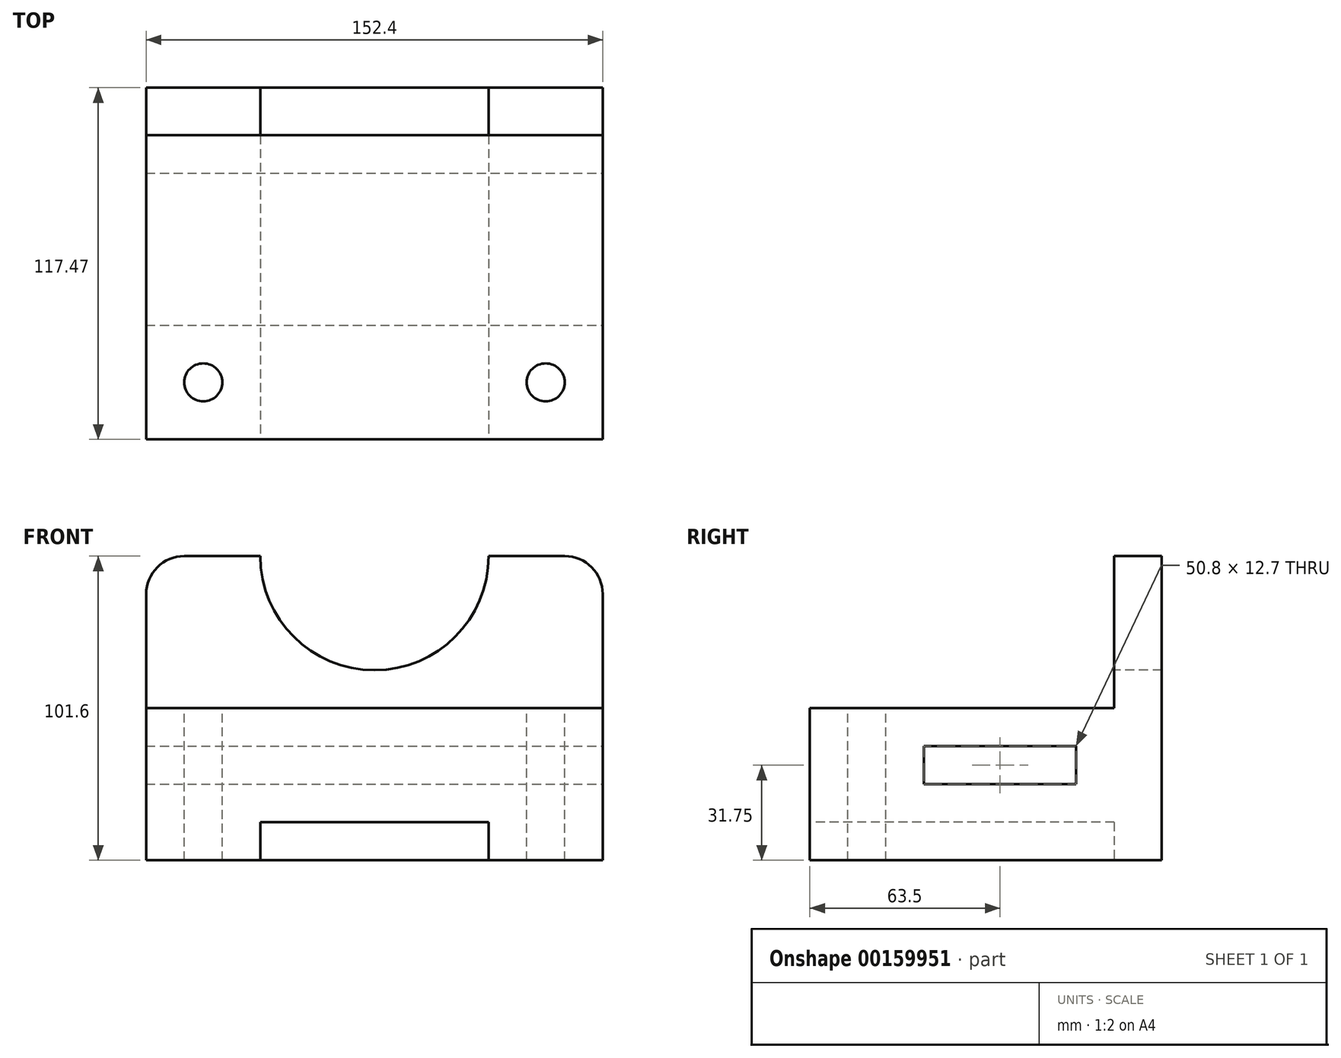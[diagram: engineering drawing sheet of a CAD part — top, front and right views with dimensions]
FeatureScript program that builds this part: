
annotation { "Feature Type Name" : "Feature", "Feature Type Description" : "" }
export const myFeature = defineFeature(function(context is Context, id is Id, definition is map)
    precondition{}
    {
        {
            var Q0;
            Q0=qCreatedBy(makeId("Front.planeOp"),FACE);
            var sketch = newSketch(context, id + "F0", { "sketchPlane" : qUnion([Q0])});
            skLineSegment(sketch, "E0.bottom", {"start": v(-76.2, 25.4) * mm, "end": v(76.2, 25.4) * mm});
            skLineSegment(sketch, "E0.top", {"start": v(-76.2, -25.4) * mm, "end": v(76.2, -25.4) * mm});
            skLineSegment(sketch, "E0.left", {"start": v(-76.2, 25.4) * mm, "end": v(-76.2, -25.4) * mm});
            skLineSegment(sketch, "E0.right", {"start": v(76.2, 25.4) * mm, "end": v(76.2, -25.4) * mm});
            skPoint(sketch, "E0.middle", {"position": v(0, 0) * mm});
            skLineSegment(sketch, "E1.bottom", {"start": v(-38.1, -12.7) * mm, "end": v(38.1, -12.7) * mm});
            skLineSegment(sketch, "E1.top", {"start": v(-38.1, -25.4) * mm, "end": v(38.1, -25.4) * mm});
            skLineSegment(sketch, "E1.left", {"start": v(-38.1, -12.7) * mm, "end": v(-38.1, -25.4) * mm});
            skLineSegment(sketch, "E1.right", {"start": v(38.1, -12.7) * mm, "end": v(38.1, -25.4) * mm});
            skSolve(sketch);
        }
        {
            var Q0;
            Q0=makeQuery(id+"F0.imprint","IMPRINT",FACE,{"disambiguationData":[TD([[makeQuery(id+"F0.imprint","IMPRINT",EDGE,{"derivedFrom":sQuery(id+"F0.wireOp",EDGE,"E0.bottom")}),-1.0]])]});
            extrude(context, id + "F1", {"entities" : qUnion([Q0]), "oppositeDirection" : true, "depth" : 101.6 * mm});
        }
        {
            var Q0;
            Q0=makeQuery(id+"F1.opExtrude","SWEPT_FACE",FACE,{"disambiguationData":[OSD([sQuery(id+"F0.wireOp",EDGE,"E0.right")])]});
            var sketch = newSketch(context, id + "F2", { "sketchPlane" : qUnion([Q0])});
            skLineSegment(sketch, "E2.bottom", {"start": v(38.1, 12.7) * mm, "end": v(88.9, 12.7) * mm});
            skLineSegment(sketch, "E2.top", {"start": v(38.1, 0) * mm, "end": v(88.9, 0) * mm});
            skLineSegment(sketch, "E2.left", {"start": v(38.1, 12.7) * mm, "end": v(38.1, 0) * mm});
            skLineSegment(sketch, "E2.right", {"start": v(88.9, 12.7) * mm, "end": v(88.9, 0) * mm});
            skLineSegment(sketch, "E3.bottom", {"start": v(53.98, 12.7) * mm, "end": v(73.03, 12.7) * mm});
            skLineSegment(sketch, "E3.top", {"start": v(53.98, 25.4) * mm, "end": v(73.03, 25.4) * mm});
            skLineSegment(sketch, "E3.left", {"start": v(53.98, 12.7) * mm, "end": v(53.98, 25.4) * mm});
            skLineSegment(sketch, "E3.right", {"start": v(73.03, 12.7) * mm, "end": v(73.03, 25.4) * mm});
            skSolve(sketch);
        }
        {
            var Q0;
            Q0=makeQuery(id+"F2.imprint","IMPRINT",FACE,{"disambiguationData":[TD([[makeQuery(id+"F2.imprint","IMPRINT",EDGE,{"derivedFrom":sQuery(id+"F2.wireOp",EDGE,"E2.bottom")}),-1.0]])]});
            var Q1;
            Q1=makeQuery(id+"F2.imprint","IMPRINT",FACE,{"disambiguationData":[TD([[makeQuery(id+"F2.imprint","IMPRINT",EDGE,{"derivedFrom":sQuery(id+"F2.wireOp",EDGE,"E3.bottom")}),1.0]])]});
            extrude(context, id + "F3", {"entities" : qUnion([Q0, Q1]), "operationType" : NewBodyOperationType.REMOVE, "oppositeDirection" : true, "depth" : 152.4 * mm});
        }
        {
            var Q0;
            {var subQ2=sQuery(id+"F0.wireOp",EDGE,"E0.bottom");Q0=makeQuery(id+"F3.boolean.opBoolean","SPLIT",FACE,{"disambiguationData":[TD([makeQuery(id+"F3.opExtrude","SWEPT_FACE",FACE,{"disambiguationData":[OSD([sQuery(id+"F2.wireOp",EDGE,"E3.left")])]})])],"derivedFrom":makeQuery(id+"F1.opExtrude","SWEPT_FACE",FACE,{"disambiguationData":[OSD([subQ2])]})});}
            var sketch = newSketch(context, id + "F4", { "sketchPlane" : qUnion([Q0])});
            skCircle(sketch, "E4", {"center": v(57.15, 19.05) * mm, "radius": 6.35 * mm});
            skLineSegment(sketch, "E5", {"start": v(0, 0) * mm, "end": v(0, 53.98) * mm, "construction": true});
            skPoint(sketch, "E5.endSnap0", {"position": v(0, 0) * mm});
            skCircle(sketch, "E6.MirrorC", {"center": v(-57.15, 19.05) * mm, "radius": 6.35 * mm});
            skSolve(sketch);
        }
        {
            var Q0;
            Q0 = qSketchRegion(id + "F4", true);
            extrude(context, id + "F5", {"entities" : qUnion([Q0]), "operationType" : NewBodyOperationType.REMOVE, "endBound" : BoundingType.UP_TO_NEXT, "oppositeDirection" : true, "depth" : 25.4 * mm});
        }
        {
            var Q0;
            {var subQ2=sQuery(id+"F0.wireOp",EDGE,"E0.bottom");Q0=makeQuery(id+"F3.boolean.opBoolean","SPLIT",FACE,{"disambiguationData":[TD([makeQuery(id+"F3.opExtrude","SWEPT_FACE",FACE,{"disambiguationData":[OSD([sQuery(id+"F2.wireOp",EDGE,"E3.right")])]})])],"derivedFrom":makeQuery(id+"F1.opExtrude","SWEPT_FACE",FACE,{"disambiguationData":[OSD([subQ2])]})});}
            var sketch = newSketch(context, id + "F6", { "sketchPlane" : qUnion([Q0])});
            skLineSegment(sketch, "E7.0", {"start": v(-76.2, 101.6) * mm, "end": v(76.2, 101.6) * mm});
            skLineSegment(sketch, "E8.top", {"start": v(-76.2, 117.47) * mm, "end": v(76.2, 117.47) * mm});
            skLineSegment(sketch, "E8.left", {"start": v(-76.2, 101.6) * mm, "end": v(-76.2, 117.47) * mm});
            skLineSegment(sketch, "E8.right", {"start": v(76.2, 101.6) * mm, "end": v(76.2, 117.48) * mm});
            skSolve(sketch);
        }
        {
            var Q0;
            Q0=makeQuery(id+"F6.imprint","IMPRINT",FACE,{"disambiguationData":[TD([[makeQuery(id+"F6.imprint","IMPRINT",EDGE,{"derivedFrom":sQuery(id+"F6.wireOp",EDGE,"E7.0")}),1.0]])]});
            extrude(context, id + "F7", {"entities" : qUnion([Q0]), "operationType" : NewBodyOperationType.ADD, "endBound" : BoundingType.SYMMETRIC, "depth" : 101.6 * mm});
        }
        {
            var Q0;
            {var subQ2=sQuery(id+"F6.wireOp",EDGE,"E7.0");Q0=makeQuery(id+"F7.boolean.opBoolean","SPLIT",FACE,{"disambiguationData":[TD([makeQuery(id+"F1.opExtrude","SWEPT_FACE",FACE,{"disambiguationData":[OSD([sQuery(id+"F0.wireOp",EDGE,"E0.bottom")])]})])],"derivedFrom":makeQuery(id+"F7.opExtrude","SWEPT_FACE",FACE,{"disambiguationData":[OSD([subQ2])]})});}
            var sketch = newSketch(context, id + "F8", { "sketchPlane" : qUnion([Q0])});
            skLineSegment(sketch, "E9.0", {"start": v(-76.2, 76.2) * mm, "end": v(76.2, 76.2) * mm});
            skArc(sketch, "E10", {"start": v(-38.1, 76.2) * mm, "mid": v(0, 38.1) * mm, "end": v(38.1, 76.2) * mm});
            skSolve(sketch);
        }
        {
            var Q0;
            {var subQ0=sQuery(id+"F8.wireOp",EDGE,"E10");Q0=makeQuery(id+"F8.imprint","IMPRINT",FACE,{"disambiguationData":[TD([[makeQuery(id+"F8.imprint","IMPRINT",EDGE,{"derivedFrom":subQ0}),1.0]])]});}
            extrude(context, id + "F9", {"entities" : qUnion([Q0]), "operationType" : NewBodyOperationType.REMOVE, "endBound" : BoundingType.UP_TO_NEXT, "oppositeDirection" : true, "depth" : 25.4 * mm});
        }
        {
            var Q0;
            Q0=makeQuery(id+"F7.opExtrude","CAP_EDGE",EDGE,{"disambiguationData":[OSD([sQuery(id+"F6.wireOp",EDGE,"E8.left")])],"isStart":false});
            var Q1;
            Q1=makeQuery(id+"F7.opExtrude","CAP_EDGE",EDGE,{"disambiguationData":[OSD([sQuery(id+"F6.wireOp",EDGE,"E8.right")])],"isStart":false});
            fillet(context, id + "F10", {"entities" : qUnion([Q0, Q1]), "radius" : 12.7 * mm, "tangentPropagation" : true, "allowEdgeOverflow" : false});
        }
    });
